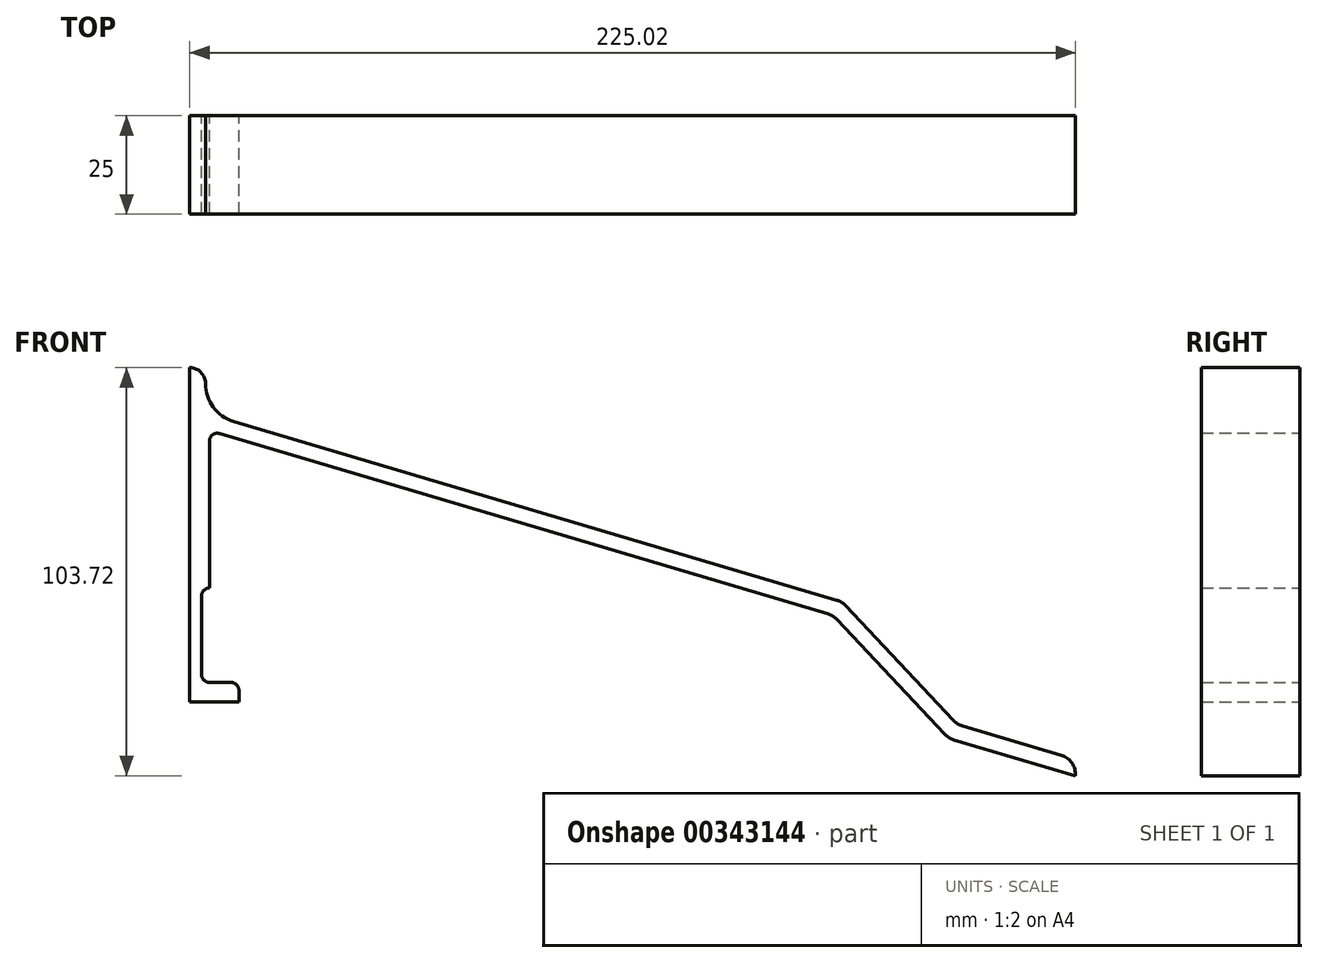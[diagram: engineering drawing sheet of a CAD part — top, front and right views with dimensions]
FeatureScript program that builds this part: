
annotation { "Feature Type Name" : "Feature", "Feature Type Description" : "" }
export const myFeature = defineFeature(function(context is Context, id is Id, definition is map)
    precondition{}
    {
        {
            var Q0;
            Q0=qCreatedBy(makeId("Front.planeOp"),FACE);
            var sketch = newSketch(context, id + "F0", { "sketchPlane" : qUnion([Q0])});
            skLineSegment(sketch, "E0", {"start": v(-64.75, -23.88) * mm, "end": v(-64.75, 61.12) * mm});
            skLineSegment(sketch, "E1", {"start": v(-64.75, -23.88) * mm, "end": v(-52.25, -23.88) * mm});
            skLineSegment(sketch, "E2", {"start": v(-52.25, -23.88) * mm, "end": v(-52.25, -20.88) * mm});
            skLineSegment(sketch, "E3", {"start": v(-54.25, -18.88) * mm, "end": v(-59.75, -18.88) * mm});
            skLineSegment(sketch, "E4", {"start": v(-61.75, -16.88) * mm, "end": v(-61.75, 3.12) * mm});
            skLineSegment(sketch, "E5", {"start": v(-59.75, 5.12) * mm, "end": v(-59.75, 5.12) * mm});
            skLineSegment(sketch, "E6", {"start": v(-59.75, 5.12) * mm, "end": v(-59.75, 42.45) * mm});
            skLineSegment(sketch, "E7", {"start": v(-57.18, 44.36) * mm, "end": v(97.5, -1.5) * mm});
            skLineSegment(sketch, "E8", {"start": v(99.72, -2.88) * mm, "end": v(127.1, -32.06) * mm});
            skLineSegment(sketch, "E9.0", {"start": v(-53.59, 47.47) * mm, "end": v(99.68, 2.02) * mm});
            skLineSegment(sketch, "E10", {"start": v(-64.75, 61.12) * mm, "end": v(-64.75, 57.12) * mm, "construction": true});
            skArc(sketch, "E11", {"start": v(-64.75, 61.12) * mm, "mid": v(-61.92, 59.95) * mm, "end": v(-60.75, 57.12) * mm});
            skLineSegment(sketch, "E12", {"start": v(-60.75, 57.12) * mm, "end": v(-60.75, 57.06) * mm});
            skArc(sketch, "E13", {"start": v(-60.75, 57.06) * mm, "mid": v(-58.76, 51.08) * mm, "end": v(-53.59, 47.47) * mm});
            skLineSegment(sketch, "E14.0", {"start": v(101.9, 0.65) * mm, "end": v(129.28, -28.53) * mm});
            skLineSegment(sketch, "E15", {"start": v(131.5, -29.9) * mm, "end": v(156.7, -37.38) * mm});
            skLineSegment(sketch, "E16.0", {"start": v(129.33, -33.43) * mm, "end": v(160.25, -42.6) * mm});
            skArc(sketch, "E17", {"start": v(156.7, -37.38) * mm, "mid": v(159.4, -39.35) * mm, "end": v(160.25, -42.6) * mm});
            skPoint(sketch, "E18.visualSharp", {"position": v(130.21, -29.52) * mm});
            skArc(sketch, "E18.filletArc", {"start": v(129.28, -28.53) * mm, "mid": v(130.3, -29.37) * mm, "end": v(131.5, -29.9) * mm});
            skPoint(sketch, "E19.visualSharp", {"position": v(128.03, -33.05) * mm});
            skArc(sketch, "E19.filletArc", {"start": v(127.1, -32.06) * mm, "mid": v(128.13, -32.9) * mm, "end": v(129.33, -33.43) * mm});
            skPoint(sketch, "E20.visualSharp", {"position": v(100.97, 1.63) * mm});
            skArc(sketch, "E20.filletArc", {"start": v(101.9, 0.65) * mm, "mid": v(100.88, 1.48) * mm, "end": v(99.68, 2.02) * mm});
            skPoint(sketch, "E21.visualSharp", {"position": v(98.8, -1.9) * mm});
            skArc(sketch, "E21.filletArc", {"start": v(99.72, -2.88) * mm, "mid": v(98.7, -2.05) * mm, "end": v(97.5, -1.5) * mm});
            skPoint(sketch, "E22.visualSharp", {"position": v(-59.75, 45.12) * mm});
            skArc(sketch, "E22.filletArc", {"start": v(-57.18, 44.36) * mm, "mid": v(-58.94, 44.05) * mm, "end": v(-59.75, 42.45) * mm});
            skPoint(sketch, "E23.visualSharp", {"position": v(-61.75, 5.12) * mm});
            skArc(sketch, "E23.filletArc", {"start": v(-59.75, 5.12) * mm, "mid": v(-61.16, 4.54) * mm, "end": v(-61.75, 3.12) * mm});
            skPoint(sketch, "E24.visualSharp", {"position": v(-61.75, -18.88) * mm});
            skArc(sketch, "E24.filletArc", {"start": v(-61.75, -16.88) * mm, "mid": v(-61.16, -18.29) * mm, "end": v(-59.75, -18.88) * mm});
            skPoint(sketch, "E25.visualSharp", {"position": v(-52.25, -18.88) * mm});
            skArc(sketch, "E25.filletArc", {"start": v(-52.25, -20.88) * mm, "mid": v(-52.83, -19.46) * mm, "end": v(-54.25, -18.88) * mm});
            skSolve(sketch);
        }
        {
            var Q0;
            Q0=makeQuery(id+"F0.imprint","IMPRINT",FACE,{"disambiguationData":[TD([[makeQuery(id+"F0.imprint","IMPRINT",EDGE,{"derivedFrom":sQuery(id+"F0.wireOp",EDGE,"E0")}),-1.0]])]});
            extrude(context, id + "F1", {"entities" : qUnion([Q0]), "depth" : 25 * mm, "offsetDistance" : 25 * mm});
        }
    });
